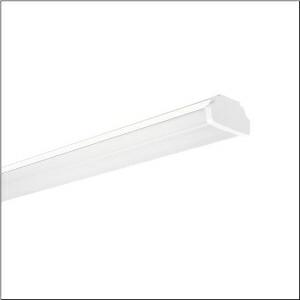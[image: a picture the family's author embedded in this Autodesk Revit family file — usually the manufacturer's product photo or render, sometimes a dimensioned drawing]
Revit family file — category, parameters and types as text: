
# Revit family: modario_r__31_ho_53bm812m1v4120_c9f3
name_source: partatom
category: Lighting Fixtures
units: mm (PartAtom-declared; Revit-internal decimal feet)

## family parameters
Cut with Voids When Loaded = No
Host = Face
Light Source = No
Part Type = Normal
Room Calculation Point = No
Round Connector Dimension = Use Diameter
Shared = No

## types (1)
- --- (1 x LED, 12380 lm, 77.3 W, 4000K)
    Apparent Load = 77 VA
    CIE Flux Codes = 47 80 95 92 100
    Color Rendering = 80
    Color Temperature = 4000K
    Default Elevation = 1800 mm
    Description = Modario® 31 HOluminaire insert, length: 1.495mm, width: 81mm, height: 82mm, LED rated luminous flux: 12.380lm, light colour: 840, control gear: ON/OFF Multilumen, control gear: ECG Multilumen, with plug, 3-pole, with phase selection, mains connection: 220..240V, AC, 50/60Hz, primary optical cover: cover, of PMMA, light emission: direct distribution, primary light characteristic: symmetric, protection rating (complete): IP20, protection rating (LED compartment): IP50, insulation class (complete): insulation class I (protective earthing), certification: CE, ENEC, VDE, permissible ambient temperature for indoor applications: -35..+35°C, corresponds to IFS (International Featured Standards) requirements for safety and quality in the food industry, reducing of maximum allowable ambient temperature of 5°C with ceiling mounting, packaging unit: 1 piece
    Height = 92 mm
    Lamp = 1 x LED
    Lamp Light Flux = 12380 lm
    Lamp Power = 77.3 W
    Lamp count = 1
    Length = 1495 mm
    Luminous efficacy = 160 lm/W
    Manufacturer = Siteco
    ModVariant = No
    Model = 53BM812M1V4120
    Mounting Place = Ceiling
    Mounting Type = Pendant
    Number of Poles = 1
    OnlyDefault = Yes
    Power Factor = 1
    Product Name = Modario® 31 HO
    Product group = luminaire insert
    ProductGroupID = 902
    Protection Class = Protection class I
    Protection Degree = IP 20
    RLX_Detail_Level = 1
    RlxData = <blob elided: 39685 chars, md5=e546bf4e>
    Socket = socket
    Standby Power = 0 W
    System Light Flux = 12380 lm
    System Power = 77 W
    Type Comments = factory setting: luminous flux: 100 % | (A | C | E) | 173 mA
    Type Image = l_1003447.jpg
    URL = http://relux.com
    VarID = @adj_133645
    Voltage = 0 V
    Weight = 0.00 kg
    Width = 81 mm

## geometry (parser evidence)
native form markers: Blend x4, Sweep x11
no freeform markers — native parametric forms only
